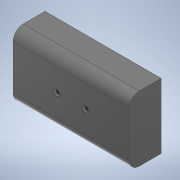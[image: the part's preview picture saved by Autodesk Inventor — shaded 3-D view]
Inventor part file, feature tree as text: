
AUTODESK INVENTOR PART (.ipt)
format: ipt  version: 2022 (Build 260153000, 153)  size: 124,928 bytes
history: native  units: mm
features: extrude x3, sketch x3, other x1, fillet x1
ambient origin geometry x8: Origin, YZ Plane, XZ Plane, XY Plane, X Axis, Y Axis, Z Axis, Center Point
bodies: Body1 (feature_tree)
feature tree (8):
  other  "ソリッド1"
  extrude  "押し出し1"  Depth=57.0mm
  fillet  "フィレット1"  Radius=32.0mm
  extrude  "押し出し2"  Depth=15.7mm TaperAngle=0.0deg
  extrude  "押し出し3"  Depth=5.0mm
  sketch  "スケッチ1"
  sketch  "スケッチ2"
  sketch  "スケッチ3"
